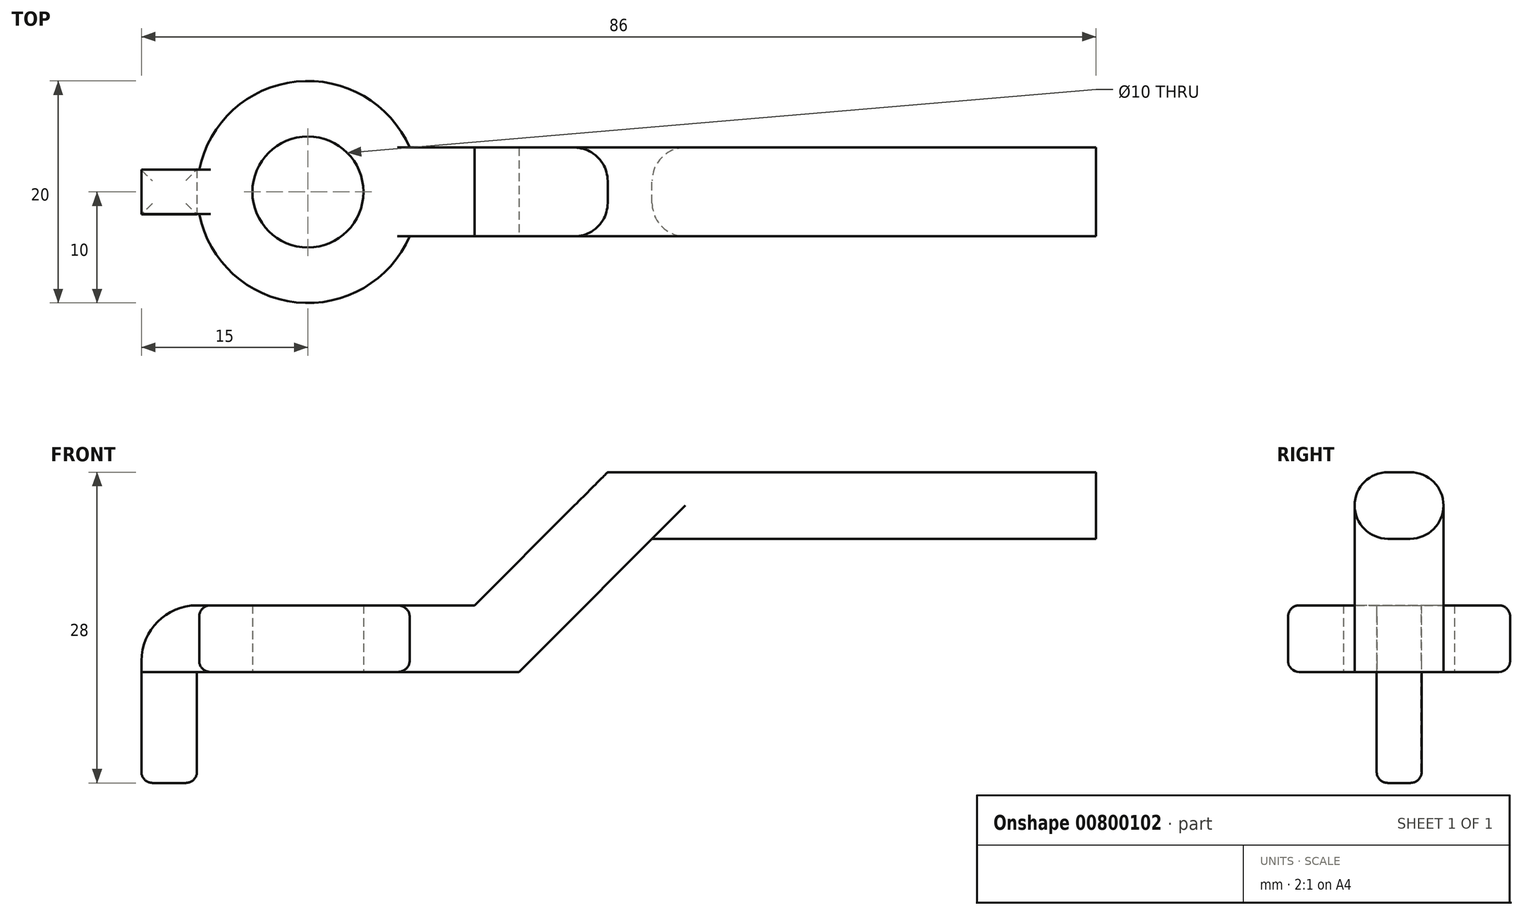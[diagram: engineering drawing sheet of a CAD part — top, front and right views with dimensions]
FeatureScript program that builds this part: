
annotation { "Feature Type Name" : "Feature", "Feature Type Description" : "" }
export const myFeature = defineFeature(function(context is Context, id is Id, definition is map)
    precondition{}
    {
        {
            var Q0;
            Q0=qCreatedBy(makeId("Top.planeOp"),FACE);
            cPlane(context, id + "F0", {"entities" : qUnion([Q0]), "cplaneType" : CPlaneType.OFFSET, "offset" : 27 * mm, "width" : 150 * mm, "height" : 150 * mm});
        }
        {
            var Q0;
            Q0=qCreatedBy(id+"F0.planeOp",FACE);
            var sketch = newSketch(context, id + "F1", { "sketchPlane" : qUnion([Q0])});
            skCircle(sketch, "E0", {"center": v(0, 0) * mm, "radius": 5 * mm});
            skCircle(sketch, "E1", {"center": v(0, 0) * mm, "radius": 10 * mm});
            skLineSegment(sketch, "E2", {"start": v(-10, 0) * mm, "end": v(-15, 0) * mm});
            skLineSegment(sketch, "E3", {"start": v(-15, 0) * mm, "end": v(-15, -2) * mm});
            skLineSegment(sketch, "E4", {"start": v(-15, -2) * mm, "end": v(-9.8, -2) * mm});
            skLineSegment(sketch, "E5", {"start": v(-15, 0) * mm, "end": v(-15, 2) * mm});
            skLineSegment(sketch, "E6", {"start": v(-15, 2) * mm, "end": v(-9.8, 2) * mm});
            skLineSegment(sketch, "E7", {"start": v(10, 0) * mm, "end": v(25, 0) * mm});
            skLineSegment(sketch, "E8", {"start": v(25, 0) * mm, "end": v(25, -4) * mm});
            skLineSegment(sketch, "E9", {"start": v(25, -4) * mm, "end": v(9.17, -4) * mm});
            skLineSegment(sketch, "E10", {"start": v(25, 0) * mm, "end": v(25, 4) * mm});
            skLineSegment(sketch, "E11", {"start": v(25, 4) * mm, "end": v(9.17, 4) * mm});
            skSolve(sketch);
        }
        {
            var Q0;
            Q0 = qSketchRegion(id + "F1", true);
            extrude(context, id + "F2", {"entities" : qUnion([Q0]), "depth" : 6 * mm, "offsetDistance" : 25 * mm});
        }
        {
            var Q0;
            Q0=qCreatedBy(id+"F0.planeOp",FACE);
            var sketch = newSketch(context, id + "F3", { "sketchPlane" : qUnion([Q0])});
            skLineSegment(sketch, "E12", {"start": v(-10, 2.03) * mm, "end": v(-10, -2.02) * mm});
            skLineSegment(sketch, "E13", {"start": v(-15, -2.02) * mm, "end": v(-15, 1.97) * mm});
            skLineSegment(sketch, "E14", {"start": v(-10, 0) * mm, "end": v(-15, 0) * mm, "construction": true});
            skLineSegment(sketch, "E15", {"start": v(0, 0) * mm, "end": v(-10, 0) * mm, "construction": true});
            skLineSegment(sketch, "E16", {"start": v(-15, -2.02) * mm, "end": v(-10, -2.02) * mm});
            skLineSegment(sketch, "E17", {"start": v(-10, 2.03) * mm, "end": v(-15, 1.97) * mm});
            skSolve(sketch);
        }
        {
            var Q0;
            Q0 = qSketchRegion(id + "F3", true);
            extrude(context, id + "F4", {"entities" : qUnion([Q0]), "operationType" : NewBodyOperationType.ADD, "oppositeDirection" : true, "depth" : 10 * mm, "offsetDistance" : 25 * mm});
        }
        {
            var Q0;
            Q0=makeQuery(id+"F2.opExtrude","CAP_EDGE",EDGE,{"disambiguationData":[OSD([sQuery(id+"F1.wireOp",EDGE,"E3"),sQuery(id+"F1.wireOp",EDGE,"E5")])],"isStart":false});
            fillet(context, id + "F5", {"entities" : qUnion([Q0]), "radius" : 5 * mm, "tangentPropagation" : true, "allowEdgeOverflow" : false});
        }
        {
            var Q0;
            Q0=makeQuery(id+"F2.opExtrude","CAP_FACE",FACE,{"disambiguationData":[OSD([sQuery(id+"F1.wireOp",EDGE,"E0"),sQuery(id+"F1.wireOp",EDGE,"E1"),sQuery(id+"F1.wireOp",EDGE,"E3"),sQuery(id+"F1.wireOp",EDGE,"E4"),sQuery(id+"F1.wireOp",EDGE,"E5"),sQuery(id+"F1.wireOp",EDGE,"E6"),sQuery(id+"F1.wireOp",EDGE,"E8"),sQuery(id+"F1.wireOp",EDGE,"E9"),sQuery(id+"F1.wireOp",EDGE,"E10"),sQuery(id+"F1.wireOp",EDGE,"E11")])],"isStart":false});
            var sketch = newSketch(context, id + "F6", { "sketchPlane" : qUnion([Q0])});
            skLineSegment(sketch, "E18", {"start": v(31, -4) * mm, "end": v(31, 4) * mm});
            skLineSegment(sketch, "E19", {"start": v(15, 4) * mm, "end": v(31, 4) * mm});
            skLineSegment(sketch, "E20", {"start": v(15, 4) * mm, "end": v(15, -4) * mm});
            skLineSegment(sketch, "E21", {"start": v(15, -4) * mm, "end": v(31, -4) * mm});
            skCircle(sketch, "E22", {"center": v(0, 0) * mm, "radius": 10 * mm, "construction": true});
            skLineSegment(sketch, "E23", {"start": v(10, 0) * mm, "end": v(15, 0) * mm, "construction": true});
            skSolve(sketch);
        }
        {
            var Q0;
            Q0 = qSketchRegion(id + "F6", true);
            extrude(context, id + "F7", {"entities" : qUnion([Q0]), "operationType" : NewBodyOperationType.ADD, "depth" : 6 * mm, "offsetDistance" : 25 * mm});
        }
        {
            var Q0;
            Q0=makeQuery(id+"F7.opExtrude","CAP_FACE",FACE,{"disambiguationData":[OSD([sQuery(id+"F6.wireOp",EDGE,"E18"),sQuery(id+"F6.wireOp",EDGE,"E19"),sQuery(id+"F6.wireOp",EDGE,"E20"),sQuery(id+"F6.wireOp",EDGE,"E21")])],"isStart":false});
            var sketch = newSketch(context, id + "F8", { "sketchPlane" : qUnion([Q0])});
            skLineSegment(sketch, "E24", {"start": v(15, 0) * mm, "end": v(21, 0) * mm, "construction": true});
            skLineSegment(sketch, "E25", {"start": v(21, 0) * mm, "end": v(21, 4) * mm});
            skLineSegment(sketch, "E26", {"start": v(21, 4) * mm, "end": v(71, 4) * mm});
            skLineSegment(sketch, "E27", {"start": v(71, 4) * mm, "end": v(71, -4) * mm});
            skLineSegment(sketch, "E28", {"start": v(71, -4) * mm, "end": v(21, -4) * mm});
            skLineSegment(sketch, "E29", {"start": v(21, -4) * mm, "end": v(21, 0) * mm});
            skSolve(sketch);
        }
        {
            var Q0;
            Q0 = qSketchRegion(id + "F8", true);
            extrude(context, id + "F9", {"entities" : qUnion([Q0]), "operationType" : NewBodyOperationType.ADD, "depth" : 6 * mm, "offsetDistance" : 25 * mm});
        }
        {
            var Q0;
            Q0=makeQuery(id+"F7.opExtrude","CAP_EDGE",EDGE,{"disambiguationData":[OSD([sQuery(id+"F6.wireOp",EDGE,"E18")])],"isStart":true});
            var Q1;
            Q1=makeQuery(id+"F2.opExtrude","CAP_EDGE",EDGE,{"disambiguationData":[OSD([sQuery(id+"F1.wireOp",EDGE,"E8"),sQuery(id+"F1.wireOp",EDGE,"E10")])],"isStart":true});
            var Q2;
            Q2=makeQuery(id+"F7.opExtrude","CAP_EDGE",EDGE,{"disambiguationData":[OSD([sQuery(id+"F6.wireOp",EDGE,"E20")])],"isStart":false});
            var Q3;
            Q3=makeQuery(id+"F9.opExtrude","CAP_EDGE",EDGE,{"disambiguationData":[OSD([sQuery(id+"F8.wireOp",EDGE,"E25"),sQuery(id+"F8.wireOp",EDGE,"E29")])],"isStart":false});
            chamfer(context, id + "F10", {"entities" : qUnion([Q0, Q1, Q2, Q3]), "width" : 6 * mm, "tangentPropagation" : true});
        }
        {
            var Q0;
            Q0=makeQuery(id+"F9.opExtrude","CAP_EDGE",EDGE,{"disambiguationData":[OSD([sQuery(id+"F8.wireOp",EDGE,"E28")])],"isStart":false});
            var Q1;
            Q1=makeQuery(id+"F9.opExtrude","CAP_EDGE",EDGE,{"disambiguationData":[OSD([sQuery(id+"F8.wireOp",EDGE,"E28")])],"isStart":true});
            var Q2;
            Q2=makeQuery(id+"F9.opExtrude","CAP_EDGE",EDGE,{"disambiguationData":[OSD([sQuery(id+"F8.wireOp",EDGE,"E26")])],"isStart":true});
            var Q3;
            Q3=makeQuery(id+"F9.opExtrude","CAP_EDGE",EDGE,{"disambiguationData":[OSD([sQuery(id+"F8.wireOp",EDGE,"E26")])],"isStart":false});
            fillet(context, id + "F11", {"entities" : qUnion([Q0, Q1, Q2, Q3]), "radius" : 3 * mm, "tangentPropagation" : true, "allowEdgeOverflow" : false});
        }
        {
            var Q0;
            {var subQ0=sQuery(id+"F1.wireOp",EDGE,"E1");Q0=makeQuery(id+"F2.opExtrude","CAP_EDGE",EDGE,{"disambiguationData":[OSD([subQ0]),TDD([makeQuery(id+"F1.imprint","IMPRINT",EDGE,{"disambiguationData":[TD([[makeQuery(id+"F1.imprint","INTERSECT",VERTEX,{"derivedFrom":[subQ0,sQuery(id+"F1.wireOp",EDGE,"E4")]}),-1.0]])],"derivedFrom":subQ0})])],"isStart":false});}
            var Q1;
            {var subQ0=sQuery(id+"F1.wireOp",EDGE,"E1");Q1=makeQuery(id+"F2.opExtrude","CAP_EDGE",EDGE,{"disambiguationData":[OSD([subQ0]),TDD([makeQuery(id+"F1.imprint","IMPRINT",EDGE,{"disambiguationData":[TD([[makeQuery(id+"F1.imprint","INTERSECT",VERTEX,{"derivedFrom":[subQ0,sQuery(id+"F1.wireOp",EDGE,"E4")]}),-1.0]])],"derivedFrom":subQ0})])],"isStart":true});}
            var Q2;
            {var subQ0=sQuery(id+"F1.wireOp",EDGE,"E1");Q2=makeQuery(id+"F2.opExtrude","CAP_EDGE",EDGE,{"disambiguationData":[OSD([subQ0]),TDD([makeQuery(id+"F1.imprint","IMPRINT",EDGE,{"disambiguationData":[TD([[makeQuery(id+"F1.imprint","INTERSECT",VERTEX,{"derivedFrom":[subQ0,sQuery(id+"F1.wireOp",EDGE,"E6")]}),1.0]])],"derivedFrom":subQ0})])],"isStart":false});}
            var Q3;
            {var subQ0=sQuery(id+"F1.wireOp",EDGE,"E1");Q3=makeQuery(id+"F2.opExtrude","CAP_EDGE",EDGE,{"disambiguationData":[OSD([subQ0]),TDD([makeQuery(id+"F1.imprint","IMPRINT",EDGE,{"disambiguationData":[TD([[makeQuery(id+"F1.imprint","INTERSECT",VERTEX,{"derivedFrom":[subQ0,sQuery(id+"F1.wireOp",EDGE,"E6")]}),1.0]])],"derivedFrom":subQ0})])],"isStart":true});}
            fillet(context, id + "F12", {"entities" : qUnion([Q0, Q1, Q2, Q3]), "radius" : 1 * mm, "tangentPropagation" : true, "allowEdgeOverflow" : false});
        }
        {
            var Q0;
            Q0=makeQuery(id+"F4.opExtrude","CAP_EDGE",EDGE,{"disambiguationData":[OSD([sQuery(id+"F3.wireOp",EDGE,"E16")])],"isStart":false});
            var Q1;
            Q1=makeQuery(id+"F4.opExtrude","CAP_EDGE",EDGE,{"disambiguationData":[OSD([sQuery(id+"F3.wireOp",EDGE,"E13")])],"isStart":false});
            var Q2;
            Q2=makeQuery(id+"F4.opExtrude","CAP_EDGE",EDGE,{"disambiguationData":[OSD([sQuery(id+"F3.wireOp",EDGE,"E17")])],"isStart":false});
            var Q3;
            Q3=makeQuery(id+"F4.opExtrude","CAP_FACE",FACE,{"disambiguationData":[OSD([sQuery(id+"F3.wireOp",EDGE,"E12"),sQuery(id+"F3.wireOp",EDGE,"E13"),sQuery(id+"F3.wireOp",EDGE,"E16"),sQuery(id+"F3.wireOp",EDGE,"E17")])],"isStart":false});
            fillet(context, id + "F13", {"entities" : qUnion([Q0, Q1, Q2, Q3]), "radius" : 1 * mm, "tangentPropagation" : true, "allowEdgeOverflow" : false});
        }
    });
